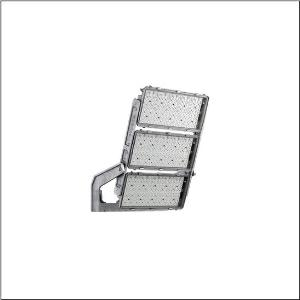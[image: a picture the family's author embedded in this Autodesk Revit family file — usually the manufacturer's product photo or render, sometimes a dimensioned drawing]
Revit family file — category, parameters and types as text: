
# Revit family: floodlight_fl_11_maxi_pro_remote___pl43_5xa779427a01ba_e28e
name_source: partatom
category: Lighting Fixtures
units: mm (PartAtom-declared; Revit-internal decimal feet)

## family parameters
Cut with Voids When Loaded = No
Host = Face
Light Source = No
Part Type = Normal
Room Calculation Point = No
Round Connector Dimension = Use Diameter
Shared = No

## types (1)
- --- (1 x LED, 151320 lm, 1095.9 W, 5000K)
    Apparent Load = 1096 VA
    CIE Flux Codes = 25 74 99 100 100
    Color Rendering = 70
    Color Temperature = 5000K
    Default Elevation = 1800 mm
    Description = Floodlight FL 11  maxi  pro Remote floodlight; light control with lens of PMMA; cover panel of toughened safety glass, transparent; light distribution: PL43, asymmetric direct distribution, LEDcolour temperature: 5000K, rated luminous flux: 151.320lm, colour rendering: CRI > 70, light colour: 750; luminous efficacy: 138lm/W; brightness control: DALI 2 (1 DALI address); with terminal, 8-pole, max. 2.5mm², mains connection: 220..240V/380..400V AC, 50/60Hz, surge voltage resistance: line to ground: 10kV, ECG replaceable separately, no afterglow with DALI off / DMX off command, LED unit replaceable without ESD environment, dustproof LED module, dimming range 10..100%; 1096W floodlight with 2x LED unit of diecast aluminium, coated grey; length: 713mm / width: 651mm / height: 338mm; mounting bracket, of diecast aluminium, uncoated, natural, equipment: Power, protection rating (complete): IP66; insulation class (complete): insulation class I (protective earthing); certification: CE, ENEC, VDE; ball protection: ball impact resistance with accessories, impact resistance: IK07; only for outdoor installations, rated ambient temperature 10°C, permissible operating ambient temperature: -40..+30°C, permissible storage temperature: -40..+85°C; packaging unit: 1 piece

Light Distribution: PL43
    Height = 320 mm
    Lamp = 1 x LED
    Lamp Light Flux = 151320 lm
    Lamp Power = 1095.9 W
    Lamp count = 1
    Length = 1002 mm
    Luminous efficacy = 138 lm/W
    Manufacturer = Siteco
    ModVariant = No
    Model = 5XA779427A01BA
    Mounting Place = Ceiling
    Mounting Type = Surface mounted
    Number of Poles = 1
    OnlyDefault = Yes
    Power Factor = 1
    Product Name = Floodlight FL 11 maxi pro Remote | PL43
    Product group = floodlight | ceiling mounted
    ProductGroupID = 302
    Protection Class = Protection class I
    Protection Degree = IP 66
    RLX_Detail_Level = 1
    RLX_Emergency_Light_Flux = 0 lm
    RLX_Emergency_Type = 0
    RLX_Emergency_Type_DB = No
    RlxData = <blob elided: 52601 chars, md5=c5e5c5ef>
    Socket = socket
    Standby Power = 0 W
    System Light Flux = 151320 lm
    System Power = 1096 W
    Type Comments = factory setting: luminous flux: 100 % | dim-lin: 254 | 760 mA
    Type Image = l_1006784.jpg
    URL = http://relux.com
    VarID = @adj_026763
    Voltage = 0 V
    Weight = 0.00 kg
    Width = 655 mm

## geometry (parser evidence)
native form markers: Blend x4, Sweep x14
no freeform markers — native parametric forms only
